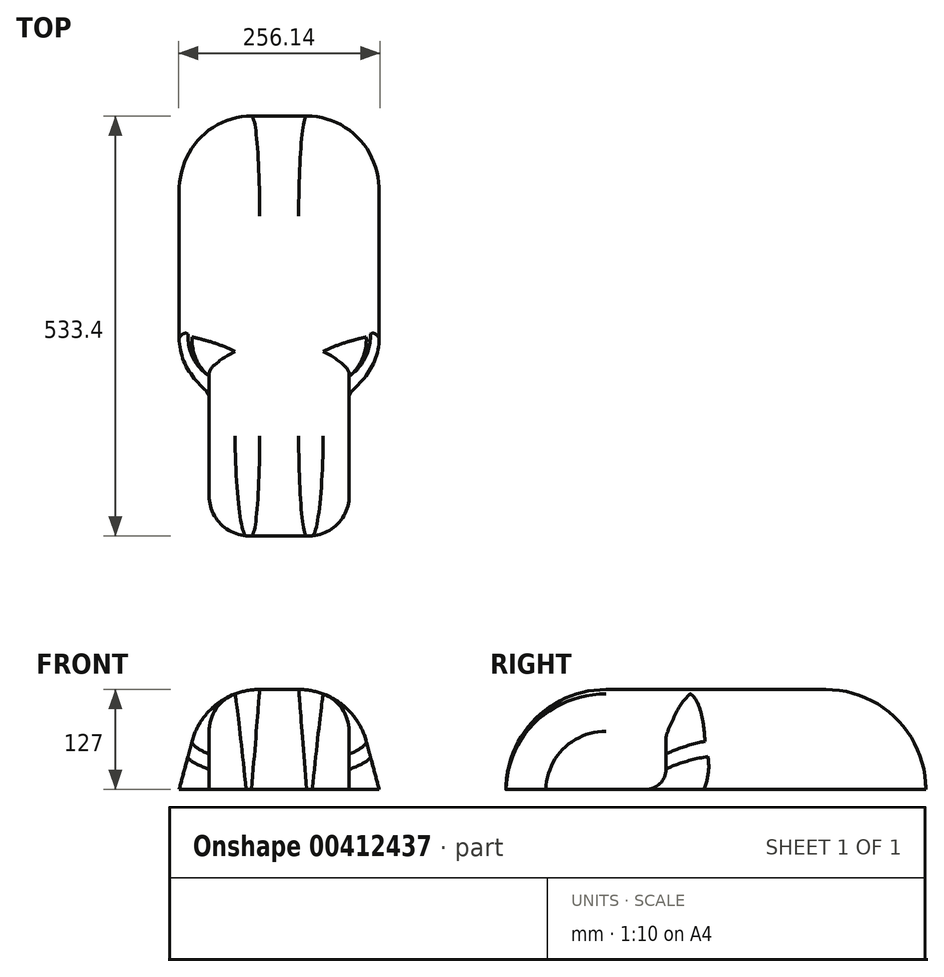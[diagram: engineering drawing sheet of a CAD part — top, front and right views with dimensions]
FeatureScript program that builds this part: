
annotation { "Feature Type Name" : "Feature", "Feature Type Description" : "" }
export const myFeature = defineFeature(function(context is Context, id is Id, definition is map)
    precondition{}
    {
        {
            var Q0;
            Q0=qCreatedBy(makeId("Front.planeOp"),FACE);
            var sketch = newSketch(context, id + "F0", { "sketchPlane" : qUnion([Q0])});
            skLineSegment(sketch, "E0", {"start": v(0, 0) * mm, "end": v(127, 0) * mm});
            skLineSegment(sketch, "E1", {"start": v(127, 0) * mm, "end": v(92.97, 127) * mm});
            skLineSegment(sketch, "E2", {"start": v(92.97, 127) * mm, "end": v(-92.97, 127) * mm});
            skLineSegment(sketch, "E3", {"start": v(-92.97, 127) * mm, "end": v(-127, 0) * mm});
            skLineSegment(sketch, "E4", {"start": v(-127, 0) * mm, "end": v(0, 0) * mm});
            skLineSegment(sketch, "E5", {"start": v(0, 0) * mm, "end": v(0, 127) * mm});
            skSolve(sketch);
        }
        {
            var Q0;
            {var subQ0=sQuery(id+"F0.wireOp",EDGE,"E3");Q0=makeQuery(id+"F0.imprint","IMPRINT",FACE,{"disambiguationData":[TD([[makeQuery(id+"F0.imprint","IMPRINT",EDGE,{"derivedFrom":subQ0}),1.0]])]});}
            var Q1;
            Q1=makeQuery(id+"F0.imprint","IMPRINT",FACE,{"disambiguationData":[TD([[makeQuery(id+"F0.imprint","IMPRINT",EDGE,{"derivedFrom":sQuery(id+"F0.wireOp",EDGE,"E0")}),1.0]])]});
            extrude(context, id + "F1", {"entities" : qUnion([Q0, Q1]), "oppositeDirection" : true, "depth" : 533.4 * mm});
        }
        {
            var Q0;
            Q0=makeQuery(id+"F1.opExtrude","CAP_EDGE",EDGE,{"disambiguationData":[OSD([sQuery(id+"F0.wireOp",EDGE,"E2")])],"isStart":true});
            var Q1;
            Q1=makeQuery(id+"F1.opExtrude","CAP_EDGE",EDGE,{"disambiguationData":[OSD([sQuery(id+"F0.wireOp",EDGE,"E2")])],"isStart":false});
            fillet(context, id + "F2", {"entities" : qUnion([Q0, Q1]), "radius" : 127 * mm, "tangentPropagation" : true, "allowEdgeOverflow" : false});
        }
        {
            var Q0;
            Q0=makeQuery(id+"F2.opFillet","BLEND_EDGE",EDGE,{"blendedFrom":[makeQuery(id+"F1.opExtrude","CAP_EDGE",EDGE,{"disambiguationData":[OSD([sQuery(id+"F0.wireOp",EDGE,"E2")])],"isStart":true}),makeQuery(id+"F1.opExtrude","SWEPT_FACE",FACE,{"disambiguationData":[OSD([sQuery(id+"F0.wireOp",EDGE,"E1")])]})],"blendedInto":[makeQuery(id+"F1.opExtrude","SWEPT_FACE",FACE,{"disambiguationData":[OSD([sQuery(id+"F0.wireOp",EDGE,"E1")])]})]});
            var Q1;
            Q1=makeQuery(id+"F1.opExtrude","SWEPT_EDGE",EDGE,{"disambiguationData":[OSD([sQuery(id+"F0.wireOp",EDGE,"E1"),sQuery(id+"F0.wireOp",EDGE,"E2")])]});
            var Q2;
            Q2=makeQuery(id+"F2.opFillet","BLEND_EDGE",EDGE,{"blendedFrom":[makeQuery(id+"F1.opExtrude","CAP_EDGE",EDGE,{"disambiguationData":[OSD([sQuery(id+"F0.wireOp",EDGE,"E2")])],"isStart":false}),makeQuery(id+"F1.opExtrude","SWEPT_FACE",FACE,{"disambiguationData":[OSD([sQuery(id+"F0.wireOp",EDGE,"E1")])]})],"blendedInto":[makeQuery(id+"F1.opExtrude","SWEPT_FACE",FACE,{"disambiguationData":[OSD([sQuery(id+"F0.wireOp",EDGE,"E1")])]})]});
            var Q3;
            Q3=makeQuery(id+"F2.opFillet","BLEND_EDGE",EDGE,{"blendedFrom":[makeQuery(id+"F1.opExtrude","CAP_EDGE",EDGE,{"disambiguationData":[OSD([sQuery(id+"F0.wireOp",EDGE,"E2")])],"isStart":true}),makeQuery(id+"F1.opExtrude","SWEPT_FACE",FACE,{"disambiguationData":[OSD([sQuery(id+"F0.wireOp",EDGE,"E3")])]})],"blendedInto":[makeQuery(id+"F1.opExtrude","SWEPT_FACE",FACE,{"disambiguationData":[OSD([sQuery(id+"F0.wireOp",EDGE,"E3")])]})]});
            var Q4;
            Q4=makeQuery(id+"F1.opExtrude","SWEPT_EDGE",EDGE,{"disambiguationData":[OSD([sQuery(id+"F0.wireOp",EDGE,"E2"),sQuery(id+"F0.wireOp",EDGE,"E3")])]});
            var Q5;
            Q5=makeQuery(id+"F2.opFillet","BLEND_EDGE",EDGE,{"blendedFrom":[makeQuery(id+"F1.opExtrude","CAP_EDGE",EDGE,{"disambiguationData":[OSD([sQuery(id+"F0.wireOp",EDGE,"E2")])],"isStart":false}),makeQuery(id+"F1.opExtrude","SWEPT_FACE",FACE,{"disambiguationData":[OSD([sQuery(id+"F0.wireOp",EDGE,"E3")])]})],"blendedInto":[makeQuery(id+"F1.opExtrude","SWEPT_FACE",FACE,{"disambiguationData":[OSD([sQuery(id+"F0.wireOp",EDGE,"E3")])]})]});
            fillet(context, id + "F3", {"entities" : qUnion([Q0, Q1, Q2, Q3, Q4, Q5]), "radius" : 88.9 * mm, "tangentPropagation" : true, "allowEdgeOverflow" : false});
        }
        {
            var Q0;
            Q0=qCreatedBy(makeId("Right.planeOp"),FACE);
            cPlane(context, id + "F4", {"entities" : qUnion([Q0]), "cplaneType" : CPlaneType.OFFSET, "offset" : 88.9 * mm, "width" : 152.4 * mm, "height" : 152.4 * mm});
        }
        {
            var Q0;
            Q0=qCreatedBy(makeId("Right.planeOp"),FACE);
            cPlane(context, id + "F5", {"entities" : qUnion([Q0]), "cplaneType" : CPlaneType.OFFSET, "offset" : 88.9 * mm, "oppositeDirection" : true, "width" : 152.4 * mm, "height" : 152.4 * mm});
        }
        {
            var Q0;
            Q0=qCreatedBy(id+"F4.planeOp",FACE);
            var sketch = newSketch(context, id + "F6", { "sketchPlane" : qUnion([Q0])});
            skLineSegment(sketch, "E6", {"start": v(0, 0) * mm, "end": v(0, 0) * mm});
            skLineSegment(sketch, "E7", {"start": v(127, 127) * mm, "end": v(152.4, 127) * mm});
            skLineSegment(sketch, "E8", {"start": v(203.2, 76.2) * mm, "end": v(203.2, 25.4) * mm});
            skLineSegment(sketch, "E9", {"start": v(177.8, 0) * mm, "end": v(0, 0) * mm});
            skPoint(sketch, "E10.visualSharp", {"position": v(0, 127) * mm});
            skArc(sketch, "E10.filletArc", {"start": v(127, 127) * mm, "mid": v(37.2, 89.8) * mm, "end": v(0, 0) * mm});
            skPoint(sketch, "E11.visualSharp", {"position": v(203.2, 127) * mm});
            skArc(sketch, "E11.filletArc", {"start": v(203.2, 76.2) * mm, "mid": v(188.32, 112.12) * mm, "end": v(152.4, 127) * mm});
            skPoint(sketch, "E12.visualSharp", {"position": v(203.2, 0) * mm});
            skArc(sketch, "E12.filletArc", {"start": v(177.8, 0) * mm, "mid": v(195.76, 7.44) * mm, "end": v(203.2, 25.4) * mm});
            skSolve(sketch);
        }
        {
            var Q0;
            Q0=makeQuery(id+"F6.imprint","IMPRINT",FACE,{"disambiguationData":[TD([[makeQuery(id+"F6.imprint","IMPRINT",EDGE,{"derivedFrom":sQuery(id+"F6.wireOp",EDGE,"E7")}),-1.0]])]});
            extrude(context, id + "F7", {"entities" : qUnion([Q0]), "operationType" : NewBodyOperationType.REMOVE, "depth" : 38.1 * mm});
        }
        {
            var Q0;
            Q0=qCreatedBy(id+"F5.planeOp",FACE);
            var sketch = newSketch(context, id + "F8", { "sketchPlane" : qUnion([Q0])});
            skLineSegment(sketch, "E13", {"start": v(0, 0) * mm, "end": v(0, 0) * mm});
            skLineSegment(sketch, "E14", {"start": v(127, 127) * mm, "end": v(152.4, 127) * mm});
            skLineSegment(sketch, "E15", {"start": v(203.2, 76.2) * mm, "end": v(203.2, 25.4) * mm});
            skLineSegment(sketch, "E16", {"start": v(177.8, 0) * mm, "end": v(0, 0) * mm});
            skPoint(sketch, "E17.visualSharp", {"position": v(0, 127) * mm});
            skArc(sketch, "E17.filletArc", {"start": v(127, 127) * mm, "mid": v(37.2, 89.8) * mm, "end": v(0, 0) * mm});
            skPoint(sketch, "E18.visualSharp", {"position": v(203.2, 127) * mm});
            skArc(sketch, "E18.filletArc", {"start": v(203.2, 76.2) * mm, "mid": v(188.32, 112.12) * mm, "end": v(152.4, 127) * mm});
            skPoint(sketch, "E19.visualSharp", {"position": v(203.2, 0) * mm});
            skArc(sketch, "E19.filletArc", {"start": v(177.8, 0) * mm, "mid": v(195.76, 7.44) * mm, "end": v(203.2, 25.4) * mm});
            skSolve(sketch);
        }
        {
            var Q0;
            Q0 = qSketchRegion(id + "F8", true);
            extrude(context, id + "F9", {"entities" : qUnion([Q0]), "operationType" : NewBodyOperationType.REMOVE, "oppositeDirection" : true, "depth" : 38.1 * mm});
        }
        {
            var Q0;
            {var subQ0=sQuery(id+"F0.wireOp",EDGE,"E2");var subQ1=sQuery(id+"F0.wireOp",EDGE,"E1");Q0=makeQuery(id+"F7.boolean.opBoolean","INTERSECT",EDGE,{"derivedFrom":[makeQuery(id+"F3.opFillet","BLEND_FACE",FACE,{"disambiguationData":[OSD([subQ1,subQ0]),TDD([makeQuery(id+"F1.opExtrude","SWEPT_EDGE",EDGE,{"disambiguationData":[OSD([subQ1,subQ0])]})])]}),makeQuery(id+"F7.opExtrude","SWEPT_FACE",FACE,{"disambiguationData":[OSD([sQuery(id+"F6.wireOp",EDGE,"E11.filletArc")])]})]});}
            var Q1;
            {var subQ0=sQuery(id+"F0.wireOp",EDGE,"E2");var subQ1=sQuery(id+"F0.wireOp",EDGE,"E1");Q1=makeQuery(id+"F7.boolean.opBoolean","INTERSECT",EDGE,{"derivedFrom":[makeQuery(id+"F3.opFillet","BLEND_FACE",FACE,{"disambiguationData":[OSD([subQ1,subQ0]),TDD([makeQuery(id+"F1.opExtrude","SWEPT_EDGE",EDGE,{"disambiguationData":[OSD([subQ1,subQ0])]})])]}),makeQuery(id+"F7.opExtrude","SWEPT_FACE",FACE,{"disambiguationData":[OSD([sQuery(id+"F6.wireOp",EDGE,"E8")])]})]});}
            var Q2;
            Q2=makeQuery(id+"F7.boolean.opBoolean","INTERSECT",EDGE,{"derivedFrom":[makeQuery(id+"F1.opExtrude","SWEPT_FACE",FACE,{"disambiguationData":[OSD([sQuery(id+"F0.wireOp",EDGE,"E1")])]}),makeQuery(id+"F7.opExtrude","SWEPT_FACE",FACE,{"disambiguationData":[OSD([sQuery(id+"F6.wireOp",EDGE,"E8")])]})]});
            var Q3;
            Q3=makeQuery(id+"F7.boolean.opBoolean","INTERSECT",EDGE,{"derivedFrom":[makeQuery(id+"F1.opExtrude","SWEPT_FACE",FACE,{"disambiguationData":[OSD([sQuery(id+"F0.wireOp",EDGE,"E1")])]}),makeQuery(id+"F7.opExtrude","SWEPT_FACE",FACE,{"disambiguationData":[OSD([sQuery(id+"F6.wireOp",EDGE,"E12.filletArc")])]})]});
            var Q4;
            {var subQ0=sQuery(id+"F0.wireOp",EDGE,"E3");var subQ1=sQuery(id+"F0.wireOp",EDGE,"E2");Q4=makeQuery(id+"F9.boolean.opBoolean","INTERSECT",EDGE,{"derivedFrom":[makeQuery(id+"F3.opFillet","BLEND_FACE",FACE,{"disambiguationData":[OSD([subQ1,subQ0]),TDD([makeQuery(id+"F1.opExtrude","SWEPT_EDGE",EDGE,{"disambiguationData":[OSD([subQ1,subQ0])]})])]}),makeQuery(id+"F9.opExtrude","SWEPT_FACE",FACE,{"disambiguationData":[OSD([sQuery(id+"F8.wireOp",EDGE,"E18.filletArc")])]})]});}
            var Q5;
            {var subQ0=sQuery(id+"F0.wireOp",EDGE,"E3");var subQ1=sQuery(id+"F0.wireOp",EDGE,"E2");Q5=makeQuery(id+"F9.boolean.opBoolean","INTERSECT",EDGE,{"derivedFrom":[makeQuery(id+"F3.opFillet","BLEND_FACE",FACE,{"disambiguationData":[OSD([subQ1,subQ0]),TDD([makeQuery(id+"F1.opExtrude","SWEPT_EDGE",EDGE,{"disambiguationData":[OSD([subQ1,subQ0])]})])]}),makeQuery(id+"F9.opExtrude","SWEPT_FACE",FACE,{"disambiguationData":[OSD([sQuery(id+"F8.wireOp",EDGE,"E15")])]})]});}
            var Q6;
            Q6=makeQuery(id+"F9.boolean.opBoolean","INTERSECT",EDGE,{"derivedFrom":[makeQuery(id+"F1.opExtrude","SWEPT_FACE",FACE,{"disambiguationData":[OSD([sQuery(id+"F0.wireOp",EDGE,"E3")])]}),makeQuery(id+"F9.opExtrude","SWEPT_FACE",FACE,{"disambiguationData":[OSD([sQuery(id+"F8.wireOp",EDGE,"E15")])]})]});
            fillet(context, id + "F10", {"entities" : qUnion([Q0, Q1, Q2, Q3, Q4, Q5, Q6]), "radius" : 63.5 * mm, "tangentPropagation" : true, "allowEdgeOverflow" : false});
        }
        {
            var Q0;
            {var subQ0=sQuery(id+"F0.wireOp",EDGE,"E2");var subQ1=sQuery(id+"F0.wireOp",EDGE,"E1");Q0=makeQuery(id+"F7.boolean.opBoolean","INTERSECT",EDGE,{"derivedFrom":[makeQuery(id+"F3.opFillet","BLEND_FACE",FACE,{"disambiguationData":[OSD([subQ1,subQ0]),TDD([makeQuery(id+"F1.opExtrude","SWEPT_EDGE",EDGE,{"disambiguationData":[OSD([subQ1,subQ0])]})])]}),makeQuery(id+"F7.opExtrude","CAP_FACE",FACE,{"disambiguationData":[OSD([sQuery(id+"F6.wireOp",EDGE,"E7"),sQuery(id+"F6.wireOp",EDGE,"E8"),sQuery(id+"F6.wireOp",EDGE,"E9"),sQuery(id+"F6.wireOp",EDGE,"E10.filletArc"),sQuery(id+"F6.wireOp",EDGE,"E11.filletArc"),sQuery(id+"F6.wireOp",EDGE,"E12.filletArc")])],"isStart":true})]});}
            var Q1;
            {var subQ0=sQuery(id+"F0.wireOp",EDGE,"E1");var subQ1=sQuery(id+"F0.wireOp",EDGE,"E2");Q1=makeQuery(id+"F7.boolean.opBoolean","INTERSECT",EDGE,{"derivedFrom":[makeQuery(id+"F3.opFillet","BLEND_FACE",FACE,{"disambiguationData":[OSD([subQ0,subQ1]),TDD([makeQuery(id+"F2.opFillet","BLEND_EDGE",EDGE,{"blendedFrom":[makeQuery(id+"F1.opExtrude","CAP_EDGE",EDGE,{"disambiguationData":[OSD([subQ1])],"isStart":true}),makeQuery(id+"F1.opExtrude","SWEPT_FACE",FACE,{"disambiguationData":[OSD([subQ0])]})],"blendedInto":[makeQuery(id+"F1.opExtrude","SWEPT_FACE",FACE,{"disambiguationData":[OSD([subQ0])]})]})])]}),makeQuery(id+"F7.opExtrude","CAP_FACE",FACE,{"disambiguationData":[OSD([sQuery(id+"F6.wireOp",EDGE,"E7"),sQuery(id+"F6.wireOp",EDGE,"E8"),sQuery(id+"F6.wireOp",EDGE,"E9"),sQuery(id+"F6.wireOp",EDGE,"E10.filletArc"),sQuery(id+"F6.wireOp",EDGE,"E11.filletArc"),sQuery(id+"F6.wireOp",EDGE,"E12.filletArc")])],"isStart":true})]});}
            var Q2;
            {var subQ0=sQuery(id+"F0.wireOp",EDGE,"E3");var subQ1=sQuery(id+"F0.wireOp",EDGE,"E2");Q2=makeQuery(id+"F9.boolean.opBoolean","INTERSECT",EDGE,{"derivedFrom":[makeQuery(id+"F3.opFillet","BLEND_FACE",FACE,{"disambiguationData":[OSD([subQ1,subQ0]),TDD([makeQuery(id+"F1.opExtrude","SWEPT_EDGE",EDGE,{"disambiguationData":[OSD([subQ1,subQ0])]})])]}),makeQuery(id+"F9.opExtrude","CAP_FACE",FACE,{"disambiguationData":[OSD([sQuery(id+"F8.wireOp",EDGE,"E14"),sQuery(id+"F8.wireOp",EDGE,"E15"),sQuery(id+"F8.wireOp",EDGE,"E16"),sQuery(id+"F8.wireOp",EDGE,"E17.filletArc"),sQuery(id+"F8.wireOp",EDGE,"E18.filletArc"),sQuery(id+"F8.wireOp",EDGE,"E19.filletArc")])],"isStart":true})]});}
            var Q3;
            {var subQ0=sQuery(id+"F0.wireOp",EDGE,"E3");var subQ1=sQuery(id+"F0.wireOp",EDGE,"E2");Q3=makeQuery(id+"F9.boolean.opBoolean","INTERSECT",EDGE,{"derivedFrom":[makeQuery(id+"F3.opFillet","BLEND_FACE",FACE,{"disambiguationData":[OSD([subQ1,subQ0]),TDD([makeQuery(id+"F2.opFillet","BLEND_EDGE",EDGE,{"blendedFrom":[makeQuery(id+"F1.opExtrude","CAP_EDGE",EDGE,{"disambiguationData":[OSD([subQ1])],"isStart":true}),makeQuery(id+"F1.opExtrude","SWEPT_FACE",FACE,{"disambiguationData":[OSD([subQ0])]})],"blendedInto":[makeQuery(id+"F1.opExtrude","SWEPT_FACE",FACE,{"disambiguationData":[OSD([subQ0])]})]})])]}),makeQuery(id+"F9.opExtrude","CAP_FACE",FACE,{"disambiguationData":[OSD([sQuery(id+"F8.wireOp",EDGE,"E14"),sQuery(id+"F8.wireOp",EDGE,"E15"),sQuery(id+"F8.wireOp",EDGE,"E16"),sQuery(id+"F8.wireOp",EDGE,"E17.filletArc"),sQuery(id+"F8.wireOp",EDGE,"E18.filletArc"),sQuery(id+"F8.wireOp",EDGE,"E19.filletArc")])],"isStart":true})]});}
            fillet(context, id + "F11", {"entities" : qUnion([Q0, Q1, Q2, Q3]), "radius" : 50.8 * mm, "tangentPropagation" : true, "allowEdgeOverflow" : false});
        }
    });
